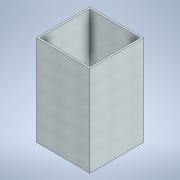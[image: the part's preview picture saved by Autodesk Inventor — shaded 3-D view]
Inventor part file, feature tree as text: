
AUTODESK INVENTOR PART (.ipt)
format: ipt  version: 2021 (Build 250183000, 183)  size: 126,464 bytes
history: native  units: mm
features: extrude x2, sketch x2
ambient origin geometry x8: Origin, YZ Plane, XZ Plane, XY Plane, X Axis, Y Axis, Z Axis, Center Point
bodies: Solid1 (feature_tree)
feature tree (4):
  extrude  "Extrusion1"  Depth=320.0mm
  extrude  "Extrusion2"  Depth=10.0mm
  sketch  "Sketch1"  dims[d0=320.0mm d1=320.0mm]
  sketch  "Sketch2"  dims[d2=540.0mm d3=0.0mm d4=10.0mm d5=10.0mm d6=10.0mm d7=10.0mm d8=530.0mm d9=0.0mm]
